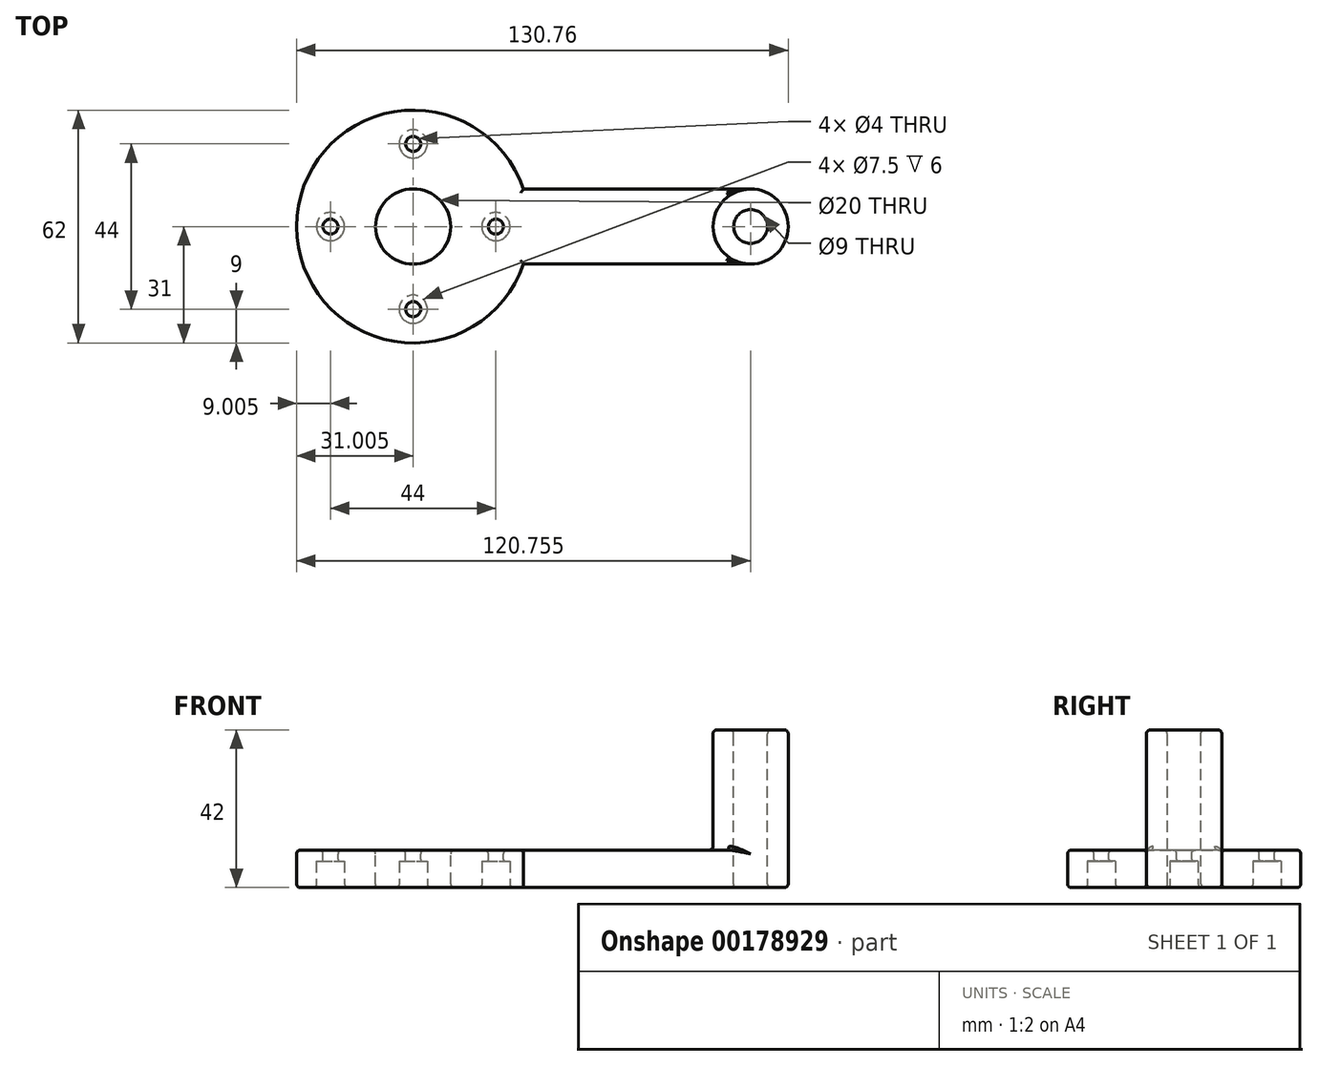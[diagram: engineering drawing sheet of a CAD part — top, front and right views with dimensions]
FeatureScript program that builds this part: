
annotation { "Feature Type Name" : "Feature", "Feature Type Description" : "" }
export const myFeature = defineFeature(function(context is Context, id is Id, definition is map)
    precondition{}
    {
        {
            var Q0;
            Q0=qCreatedBy(makeId("Top.planeOp"),FACE);
            var sketch = newSketch(context, id + "F0", { "sketchPlane" : qUnion([Q0])});
            skLineSegment(sketch, "E0", {"start": v(0, 0) * mm, "end": v(44.88, 0) * mm, "construction": true});
            skLineSegment(sketch, "E1", {"start": v(0, 0) * mm, "end": v(-44.88, 0) * mm, "construction": true});
            skCircle(sketch, "E2", {"center": v(-44.88, 0) * mm, "radius": 4.5 * mm});
            skCircle(sketch, "E3", {"center": v(44.88, 0) * mm, "radius": 4.5 * mm});
            skCircle(sketch, "E4", {"center": v(-44.88, 0) * mm, "radius": 10 * mm});
            skCircle(sketch, "E5", {"center": v(44.88, 0) * mm, "radius": 10 * mm});
            skLineSegment(sketch, "E6", {"start": v(-44.88, 10) * mm, "end": v(44.88, 10) * mm});
            skLineSegment(sketch, "E7", {"start": v(-44.88, -10) * mm, "end": v(44.88, -10) * mm});
            skCircle(sketch, "E8", {"center": v(-44.88, 0) * mm, "radius": 31 * mm});
            skCircle(sketch, "E9", {"center": v(-44.88, 0) * mm, "radius": 22 * mm, "construction": true});
            skPoint(sketch, "E10", {"position": v(-44.88, 22) * mm});
            skPoint(sketch, "E11", {"position": v(-66.87, 0) * mm});
            skPoint(sketch, "E12", {"position": v(-44.88, -22) * mm});
            skPoint(sketch, "E13", {"position": v(-22.88, 0) * mm});
            skCircle(sketch, "E14", {"center": v(-44.88, 22) * mm, "radius": 2 * mm});
            skCircle(sketch, "E15", {"center": v(-66.87, 0) * mm, "radius": 2 * mm});
            skCircle(sketch, "E16", {"center": v(-44.88, -22) * mm, "radius": 2 * mm});
            skCircle(sketch, "E17", {"center": v(-22.88, 0) * mm, "radius": 2 * mm});
            skSolve(sketch);
        }
        {
            var Q0;
            Q0=qSketchRegion(id+"F0",true);
            extrude(context, id + "F1", {"entities" : qUnion([Q0]), "oppositeDirection" : true, "depth" : 10 * mm});
        }
        {
            var Q0;
            Q0=makeQuery(id+"F0.imprint","IMPRINT",FACE,{"disambiguationData":[TD([[makeQuery(id+"F0.imprint","IMPRINT",EDGE,{"derivedFrom":sQuery(id+"F0.wireOp",EDGE,"E3")}),-1.0]])]});
            extrude(context, id + "F2", {"entities" : qUnion([Q0]), "operationType" : NewBodyOperationType.ADD, "depth" : 32 * mm});
        }
        {
            var Q0;
            Q0=makeQuery(id+"F1.opExtrude","CAP_FACE",FACE,{"disambiguationData":[OSD([sQuery(id+"F0.wireOp",EDGE,"E3"),sQuery(id+"F0.wireOp",EDGE,"E4"),sQuery(id+"F0.wireOp",EDGE,"E5"),sQuery(id+"F0.wireOp",EDGE,"E6"),sQuery(id+"F0.wireOp",EDGE,"E7"),sQuery(id+"F0.wireOp",EDGE,"E8"),sQuery(id+"F0.wireOp",EDGE,"E14"),sQuery(id+"F0.wireOp",EDGE,"E15"),sQuery(id+"F0.wireOp",EDGE,"E16"),sQuery(id+"F0.wireOp",EDGE,"E17")])],"isStart":false});
            var sketch = newSketch(context, id + "F3", { "sketchPlane" : qUnion([Q0])});
            skCircle(sketch, "E18", {"center": v(-44.88, 22) * mm, "radius": 3.75 * mm});
            skCircle(sketch, "E19", {"center": v(-22.88, 0) * mm, "radius": 3.75 * mm});
            skCircle(sketch, "E20", {"center": v(-44.88, -22) * mm, "radius": 3.75 * mm});
            skCircle(sketch, "E21", {"center": v(-66.87, 0) * mm, "radius": 3.75 * mm});
            skSolve(sketch);
        }
        {
            var Q0;
            Q0 = qSketchRegion(id + "F3", true);
            extrude(context, id + "F4", {"entities" : qUnion([Q0]), "operationType" : NewBodyOperationType.REMOVE, "oppositeDirection" : true, "depth" : 7 * mm});
        }
        {
            var Q0;
            Q0=makeQuery(id+"F2.opExtrude","CAP_FACE",FACE,{"disambiguationData":[OSD([sQuery(id+"F0.wireOp",EDGE,"E2"),sQuery(id+"F0.wireOp",EDGE,"E4")])],"isStart":false});
            var Q1;
            Q1=makeQuery(id+"F1.opExtrude","CAP_FACE",FACE,{"disambiguationData":[OSD([sQuery(id+"F0.wireOp",EDGE,"E2"),sQuery(id+"F0.wireOp",EDGE,"E3"),sQuery(id+"F0.wireOp",EDGE,"E4"),sQuery(id+"F0.wireOp",EDGE,"E5"),sQuery(id+"F0.wireOp",EDGE,"E6"),sQuery(id+"F0.wireOp",EDGE,"E7")])],"isStart":true});
            var Q2;
            Q2=makeQuery(id+"F2.opExtrude","CAP_FACE",FACE,{"disambiguationData":[OSD([sQuery(id+"F0.wireOp",EDGE,"E3"),sQuery(id+"F0.wireOp",EDGE,"E5")])],"isStart":false});
            var Q3;
            Q3=makeQuery(id+"F1.opExtrude","CAP_FACE",FACE,{"disambiguationData":[OSD([sQuery(id+"F0.wireOp",EDGE,"E2"),sQuery(id+"F0.wireOp",EDGE,"E3"),sQuery(id+"F0.wireOp",EDGE,"E4"),sQuery(id+"F0.wireOp",EDGE,"E5"),sQuery(id+"F0.wireOp",EDGE,"E6"),sQuery(id+"F0.wireOp",EDGE,"E7")])],"isStart":false});
            fillet(context, id + "F5", {"entities" : qUnion([Q0, Q1, Q2, Q3]), "radius" : 1 * mm, "tangentPropagation" : true, "allowEdgeOverflow" : false});
        }
        {
            var Q0;
            Q0=makeQuery(id+"F1.opExtrude","SWEPT_FACE",FACE,{"disambiguationData":[OSD([sQuery(id+"F0.wireOp",EDGE,"E15")])]});
            var Q1;
            Q1=makeQuery(id+"F1.opExtrude","SWEPT_FACE",FACE,{"disambiguationData":[OSD([sQuery(id+"F0.wireOp",EDGE,"E16")])]});
            var Q2;
            Q2=makeQuery(id+"F1.opExtrude","SWEPT_FACE",FACE,{"disambiguationData":[OSD([sQuery(id+"F0.wireOp",EDGE,"E17")])]});
            var Q3;
            Q3=makeQuery(id+"F1.opExtrude","SWEPT_FACE",FACE,{"disambiguationData":[OSD([sQuery(id+"F0.wireOp",EDGE,"E14")])]});
            fillet(context, id + "F6", {"entities" : qUnion([Q0, Q1, Q2, Q3]), "radius" : .5 * mm, "tangentPropagation" : true, "allowEdgeOverflow" : false});
        }
    });
